# Revit family: JC KONTAKTER JCK217 DE
name_source: partatom
category: Specialty Equipment
units: mm (PartAtom-declared; Revit-internal decimal feet)

## family parameters
Cut with Voids When Loaded = No
Enable Cutting in Views = Yes
Host = Face
Maintain Annotation Orientation = Yes
Part Type = Normal
Room Calculation Point = No
Round Connector Dimension = Use Diameter
Shared = No

## types (1)
- JCK217
    Anzahl der mikroschalter = 1
    CE-kennzeichnung = https://jckontakter.se
    Deckel = Aluminum ENAW 6060-T6 (schwarz)
    Default Elevation = 800 mm  [stored 2.62467 ft]
    Description = Großflächentaster aus schwarzeloxiertem Aluminium mit weißen Kunststoff-Endkappen. Die vier Tastlinien auf der Tastfläche zeigen an, wo der Taster zum Aktivieren der Türöffnung gedrückt werden muss. Mit einem feuchtigkeitsgeschützten Mikroschalter der IP-Klasse 67 ausgestattet. Für den Einsatz in Innen- und Außenbereichen geeignet.
    Endkappen = POM kunststoff (weiss)
    Geringster nennstrom = 1mA/4 V DC
    Herstellungsland = Schweden
    Kern = Aluminum 6060-T6
    Manufacturer = JC kontakter
    Mikroschalter = Standard NO IP67
    Model = JCK217
    Nomineller nennstrom = 12 V - Resistive 6A Inductive L/R 5ms 6A, 24 V - Resistive 6A Inductive L/R 5ms 5A
    Produktgewicht = 0.305 kg.
    Technisches Produktblatt = https://grossflaechentaster.de
    URL = https://grossflaechentaster.de

note: [stored X ft] marks values corroborated as IEEE doubles in the binary element streams (Revit-internal decimal feet)

## geometry (parser evidence)
native form markers: Sweep x5
no freeform markers — native parametric forms only
